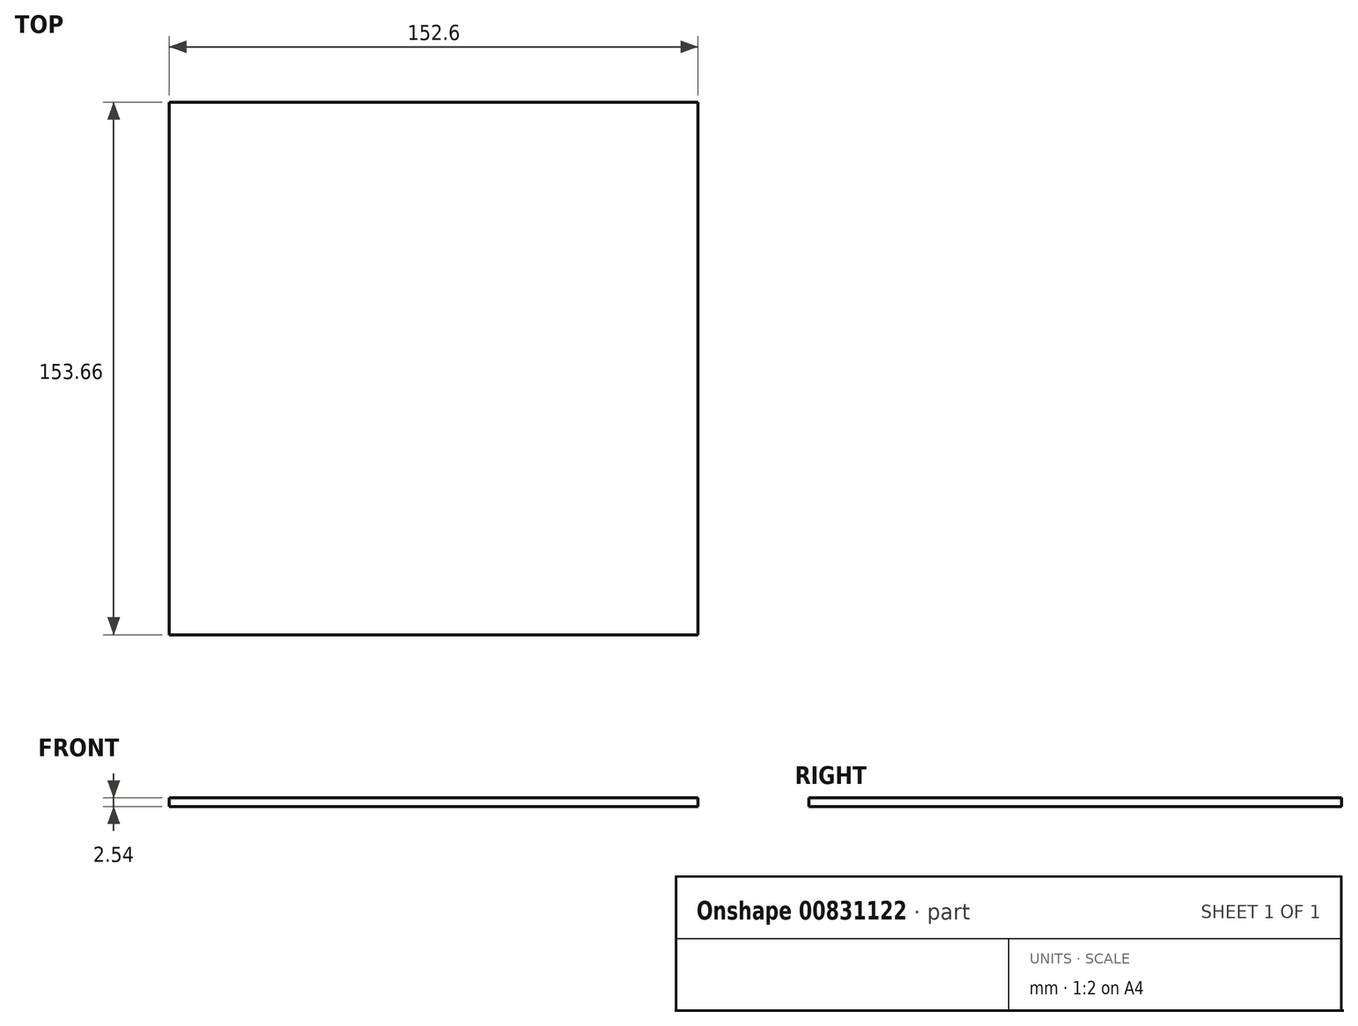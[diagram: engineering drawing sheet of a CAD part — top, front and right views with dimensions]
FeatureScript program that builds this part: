
annotation { "Feature Type Name" : "Feature", "Feature Type Description" : "" }
export const myFeature = defineFeature(function(context is Context, id is Id, definition is map)
    precondition{}
    {
        {
            var Q0;
            Q0=qCreatedBy(makeId("Top.planeOp"),FACE);
            var sketch = newSketch(context, id + "F0", { "sketchPlane" : qUnion([Q0])});
            skLineSegment(sketch, "E0.bottom", {"start": v(-77.23, 77.5) * mm, "end": v(75.37, 77.5) * mm});
            skLineSegment(sketch, "E0.top", {"start": v(-77.23, -76.17) * mm, "end": v(75.37, -76.17) * mm});
            skLineSegment(sketch, "E0.left", {"start": v(-77.23, 77.5) * mm, "end": v(-77.23, -76.17) * mm});
            skLineSegment(sketch, "E0.right", {"start": v(75.37, 77.5) * mm, "end": v(75.37, -76.17) * mm});
            skSolve(sketch);
        }
        {
            var Q0;
            Q0=qSketchRegion(id+"F0",true);
            extrude(context, id + "F1", {"entities" : qUnion([Q0]), "depth" : 2.54 * mm, "offsetDistance" : 25.4 * mm});
        }
    });
